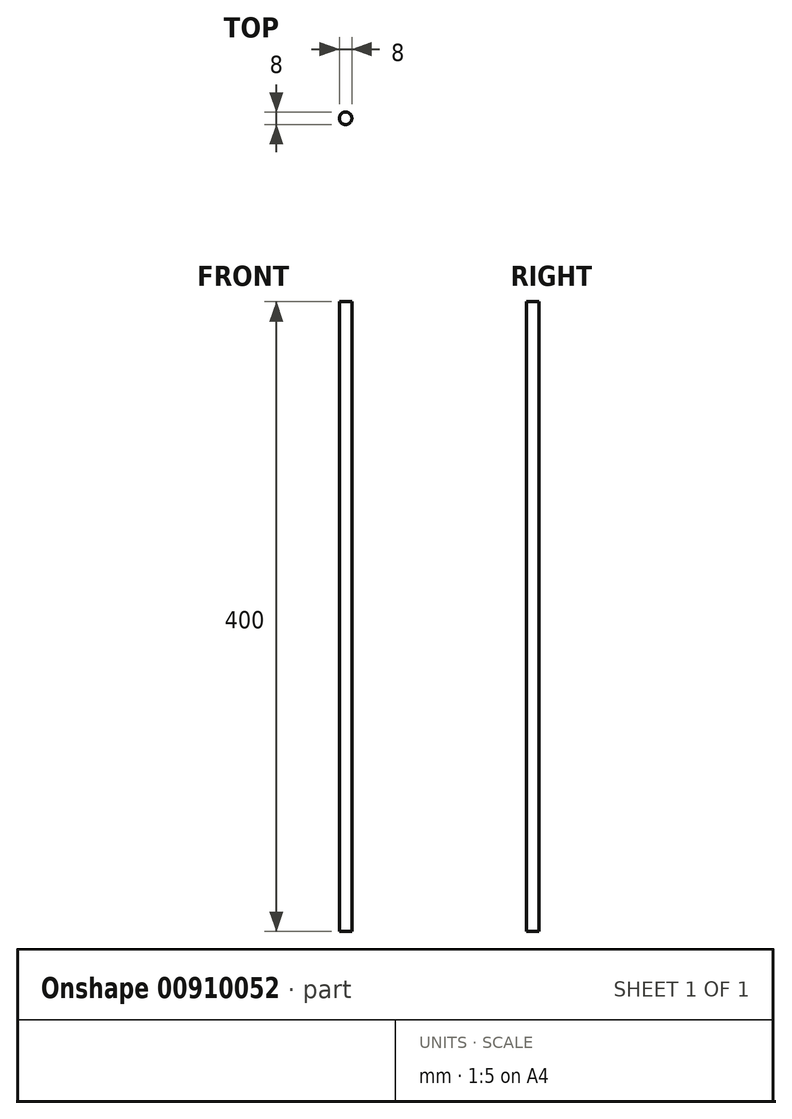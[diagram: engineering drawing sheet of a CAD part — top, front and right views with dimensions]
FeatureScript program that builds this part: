
annotation { "Feature Type Name" : "Feature", "Feature Type Description" : "" }
export const myFeature = defineFeature(function(context is Context, id is Id, definition is map)
    precondition{}
    {
        {
            var Q0;
            Q0=qCreatedBy(makeId("Top.planeOp"),FACE);
            var sketch = newSketch(context, id + "F0", { "sketchPlane" : qUnion([Q0])});
            skCircle(sketch, "E0", {"center": v(0, 0) * mm, "radius": 4 * mm});
            skSolve(sketch);
        }
        {
            var Q0;
            Q0=makeQuery(id+"F0.imprint","IMPRINT",FACE,{"disambiguationData":[TD([[makeQuery(id+"F0.imprint","IMPRINT",EDGE,{"derivedFrom":sQuery(id+"F0.wireOp",EDGE,"E0")}),1.0]])]});
            extrude(context, id + "F1", {"entities" : qUnion([Q0]), "depth" : 400 * mm, "offsetDistance" : 25 * mm});
        }
    });
